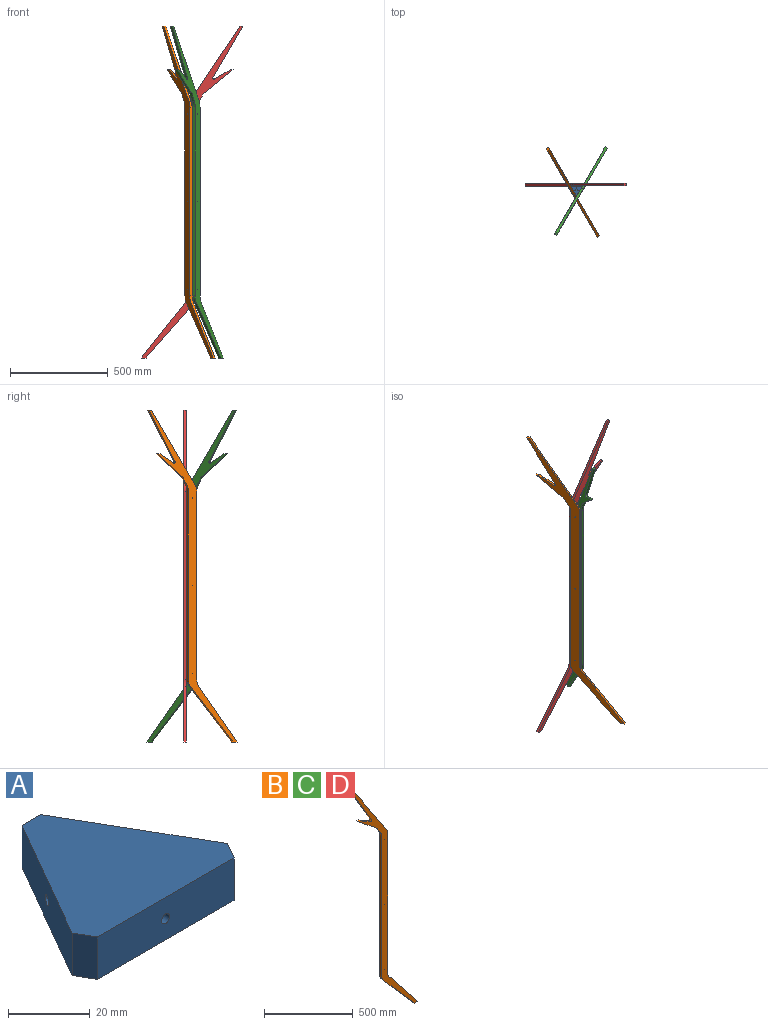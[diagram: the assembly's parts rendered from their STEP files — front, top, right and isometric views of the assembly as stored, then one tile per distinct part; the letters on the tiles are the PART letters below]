
ASSEMBLY  parts=4 mates=3
PART A: 14 faces, bbox 53.7x46.5x12.7 mm
  f0: plane 40.96x23.65mm, normal (0.87,0.5,0), area 594.6mm2, adj f3,f4,f5,f6,f12
  f1: plane 40.96x23.65mm, normal (-0.87,0.5,0), area 594.6mm2, adj f3,f4,f5,f7,f10
  f2: plane 47.3x12.7mm, normal (0,-1,0), area 594.6mm2, adj f3,f4,f6,f7,f8
  f3: plane 53.65x46.46mm, normal (0,0,1), area 1506.5mm2, adj f0,f1,f2,f5,f6,f7
  f4: plane 53.65x46.46mm, normal (0,0,-1), area 1506.5mm2, adj f0,f1,f2,f5,f6,f7
  f5: plane 12.7x6.35mm, normal (0,1,0), area 80.6mm2, adj f0,f1,f3,f4
  f6: plane 12.7x5.5mm, normal (0.87,-0.5,0), area 80.6mm2, adj f0,f2,f3,f4
  f7: plane 12.7x5.5mm, normal (-0.87,-0.5,0), area 80.6mm2, adj f1,f2,f3,f4
  f8: cylinder r=1.39mm len=12.7mm, axis (0,-1,0), area 110.8mm2, adj f2,f9
  f9: plane 2.78x2.78mm, normal (0,-1,0), area 6.1mm2, adj f8
  f10: cylinder r=1.39mm len=12.39mm, axis (-0.87,0.5,0), area 110.8mm2, adj f1,f11
  f11: plane 2.78x2.41mm, normal (-0.87,0.5,0), area 6.1mm2, adj f10
  f12: cylinder r=1.39mm len=12.39mm, axis (0.87,0.5,0), area 110.8mm2, adj f0,f13
  f13: plane 2.78x2.41mm, normal (0.87,0.5,0), area 6.1mm2, adj f12
PART B: 23 faces, bbox 520x12.7x1700 mm
  f0: plane 286.14x226.53mm, normal (0.78,0,0.62), area 4634.9mm2, adj f11,f12,f13,f14
  f1: plane 966.9x12.7mm, normal (1,0,0), area 12279.7mm2, adj f12,f13,f14,f15
  f2: plane 387.18x258.93mm, normal (0.83,0,0.56), area 5915.4mm2, adj f3,f12,f13,f15
  f3: plane 15x12.7mm, normal (0,0,1), area 190.5mm2, adj f2,f4,f12,f13
  f4: plane 262.52x152.59mm, normal (-0.86,0,-0.5), area 3856.3mm2, adj f3,f12,f13,f22
  f5: plane 78.89x46.19mm, normal (0.51,0,0.86), area 1161mm2, adj f6,f12,f13,f22
  f6: plane 15x12.7mm, normal (0,0,1), area 190.5mm2, adj f5,f7,f12,f13
  f7: plane 142.94x113.85mm, normal (-0.62,0,-0.78), area 2320.8mm2, adj f6,f12,f13,f16
  f8: plane 35.11x20.41mm, normal (-0.86,0,-0.5), area 515.7mm2, adj f12,f13,f16,f17
  f9: plane 967.22x12.7mm, normal (-1,0,0), area 12283.7mm2, adj f12,f13,f17,f18
  f10: plane 285.64x249.93mm, normal (-0.75,0,-0.66), area 4820.2mm2, adj f11,f12,f13,f18
  f11: plane 25x12.7mm, normal (0,0,-1), area 317.5mm2, adj f0,f10,f12,f13
  f12: plane 1700x520mm, normal (0,-1,0), area 77246mm2, adj f0,f1,f2,f3,f4,f5,f6,f7
  f13: plane 1700x520mm, normal (0,1,0), area 77246mm2, adj f0,f1,f2,f3,f4,f5,f6,f7
  f14: cylinder r=50.8mm len=31.53mm, axis (0,-1,0), area 432mm2, adj f0,f1,f12,f13
  f15: cylinder r=50.8mm len=28.24mm, axis (0,1,0), area 380.3mm2, adj f1,f2,f12,f13
  f16: cylinder r=50.8mm len=14.21mm, axis (0,1,0), area 239.8mm2, adj f7,f8,f12,f13
  f17: cylinder r=50.8mm len=25.53mm, axis (0,1,0), area 339.7mm2, adj f8,f9,f12,f13
  f18: cylinder r=50.8mm len=33.45mm, axis (0,-1,0), area 463.8mm2, adj f9,f10,f12,f13
  f19: cylinder r=1.19mm len=12.7mm, axis (0,-1,0), area 95mm2, adj f12,f13
  f20: cylinder r=1.19mm len=12.7mm, axis (0,-1,0), area 95mm2, adj f12,f13
  f21: cylinder r=1.19mm len=12.7mm, axis (0,-1,0), area 95mm2, adj f12,f13
  f22: cylinder r=6.35mm len=12.7mm, axis (0,-1,0), area 211.9mm2, adj f4,f5,f12,f13
PART C: same geometry as B
PART D: same geometry as B
PLACE A rot(axis=(1,0,0),180deg) t=(0,-8.66,0)mm
PLACE B rot(axis=(0,0,-1),60deg) t=(-15,-8.66,-6.35)mm
PLACE C rot(axis=(0,0,1),60deg) t=(15,-8.66,-6.35)mm
PLACE D rot(axis=(0,0,1),180deg) t=(0,17.32,-6.35)mm
MATE fastened D.f19 <-> A.f8  axis (0,-1,0) through (0,17.32,-6.35)mm
MATE fastened C.f19 <-> A.f12  axis (-0.87,0.5,0) through (15,-8.66,-6.35)mm
MATE fastened B.f19 <-> A.f10  axis (0.87,0.5,0) through (-15,-8.66,-6.35)mm
